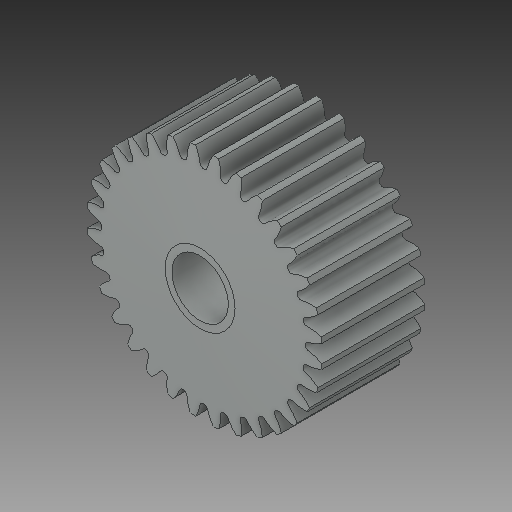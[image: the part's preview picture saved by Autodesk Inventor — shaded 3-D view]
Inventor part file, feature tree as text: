
AUTODESK INVENTOR PART (.ipt)
format: ipt  version: 2017 (Build 210142000, 142)  size: 510,976 bytes
history: native  units: in
note: dims shown in document units (in); Inventor stores cm internally (conversion verified against a paired STEP export)
features: mirror x1
ambient origin geometry x8: Origin, YZ Plane, XZ Plane, XY Plane, X Axis, Y Axis, Z Axis, Center Point
bodies: Solid1 (feature_tree)
feature tree (1):
  mirror  "Mirror1"
